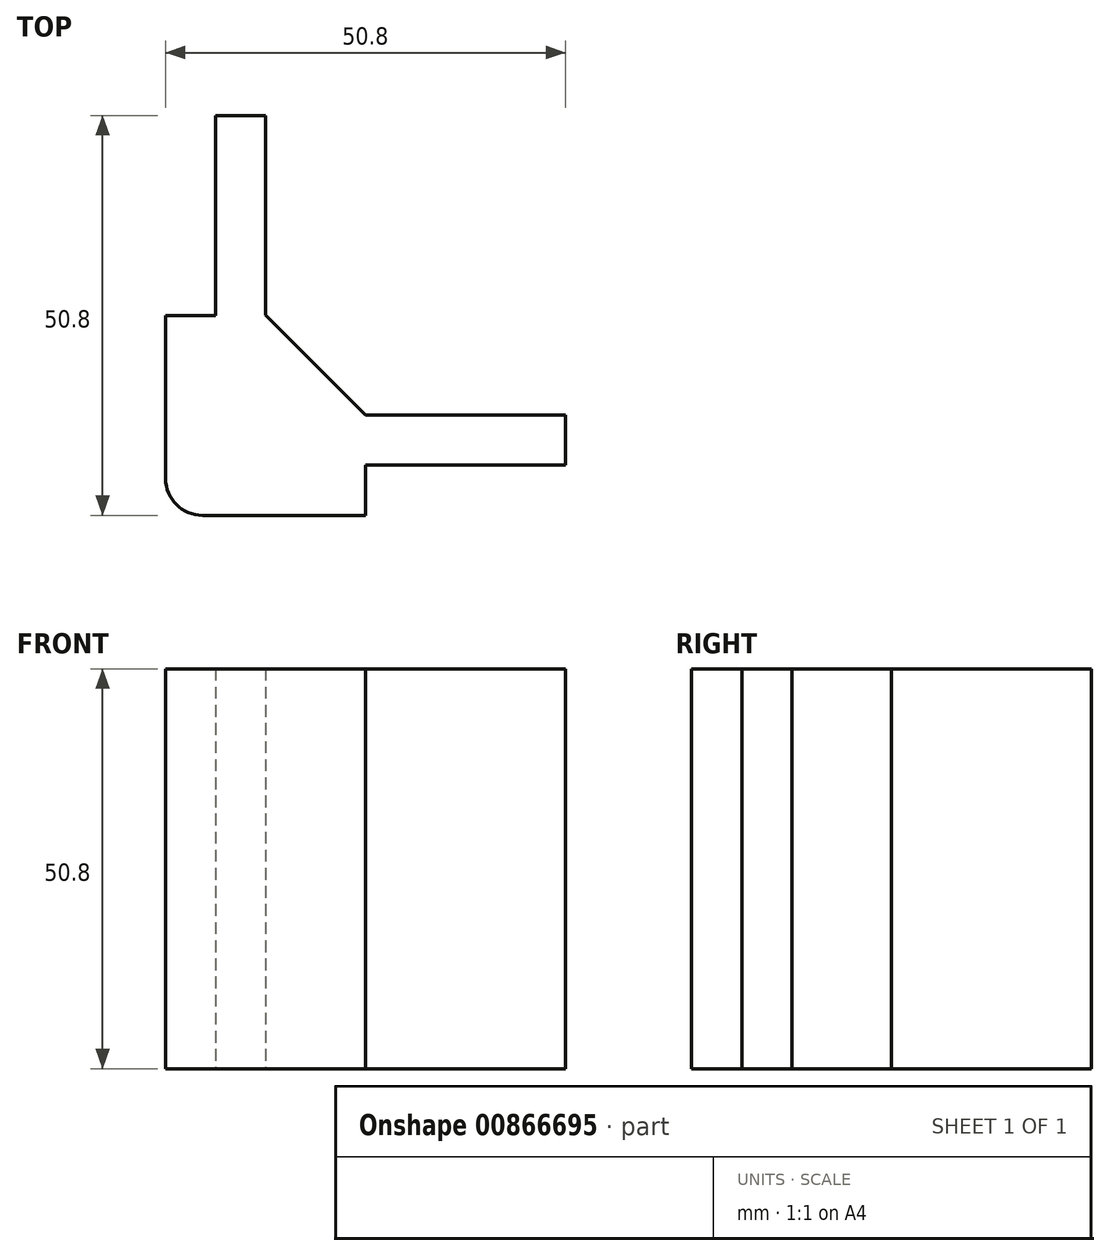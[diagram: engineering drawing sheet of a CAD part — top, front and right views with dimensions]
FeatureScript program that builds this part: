
annotation { "Feature Type Name" : "Feature", "Feature Type Description" : "" }
export const myFeature = defineFeature(function(context is Context, id is Id, definition is map)
    precondition{}
    {
        {
            var Q0;
            Q0=qCreatedBy(makeId("Top.planeOp"),FACE);
            var sketch = newSketch(context, id + "F0", { "sketchPlane" : qUnion([Q0])});
            skLineSegment(sketch, "E0", {"start": v(4.33, 42.13) * mm, "end": v(4.33, 16.73) * mm});
            skLineSegment(sketch, "E1", {"start": v(42.43, 4.08) * mm, "end": v(17.03, 4.08) * mm});
            skLineSegment(sketch, "E2", {"start": v(17.03, 4.08) * mm, "end": v(4.33, 16.73) * mm});
            skLineSegment(sketch, "E3", {"start": v(42.43, -2.27) * mm, "end": v(17.03, -2.27) * mm});
            skLineSegment(sketch, "E4", {"start": v(17.03, -2.27) * mm, "end": v(17.03, -8.67) * mm});
            skLineSegment(sketch, "E5", {"start": v(-2.02, 42.13) * mm, "end": v(-2.02, 16.73) * mm});
            skLineSegment(sketch, "E6", {"start": v(-2.02, 16.73) * mm, "end": v(-8.37, 16.73) * mm});
            skLineSegment(sketch, "E7", {"start": v(-8.37, 16.73) * mm, "end": v(-8.37, -4) * mm});
            skLineSegment(sketch, "E8", {"start": v(17.03, -8.67) * mm, "end": v(-3.7, -8.67) * mm});
            skLineSegment(sketch, "E9", {"start": v(-2.02, 42.13) * mm, "end": v(4.33, 42.13) * mm});
            skLineSegment(sketch, "E10", {"start": v(42.43, -2.27) * mm, "end": v(42.43, 4.08) * mm});
            skPoint(sketch, "E11.visualSharp", {"position": v(-8.37, -8.67) * mm});
            skArc(sketch, "E11.filletArc", {"start": v(-8.37, -4) * mm, "mid": v(-7, -7.3) * mm, "end": v(-3.7, -8.67) * mm});
            skSolve(sketch);
        }
        {
            var Q0;
            Q0 = qSketchRegion(id + "F0", true);
            extrude(context, id + "F1", {"entities" : qUnion([Q0]), "depth" : 50.8 * mm, "offsetDistance" : 25.4 * mm});
        }
        {
            var Q0;
            Q0=makeQuery(id+"F1.opExtrude","CAP_FACE",FACE,{"disambiguationData":[OSD([sQuery(id+"F0.wireOp",EDGE,"E0"),sQuery(id+"F0.wireOp",EDGE,"E1"),sQuery(id+"F0.wireOp",EDGE,"E2"),sQuery(id+"F0.wireOp",EDGE,"E3"),sQuery(id+"F0.wireOp",EDGE,"E4"),sQuery(id+"F0.wireOp",EDGE,"E5"),sQuery(id+"F0.wireOp",EDGE,"E6"),sQuery(id+"F0.wireOp",EDGE,"E7"),sQuery(id+"F0.wireOp",EDGE,"E8"),sQuery(id+"F0.wireOp",EDGE,"E9"),sQuery(id+"F0.wireOp",EDGE,"E10"),sQuery(id+"F0.wireOp",EDGE,"E11.filletArc")])],"isStart":true});
            cPlane(context, id + "F2", {"entities" : qUnion([Q0]), "cplaneType" : CPlaneType.OFFSET, "offset" : 12.7 * mm, "oppositeDirection" : true, "width" : 152.4 * mm, "height" : 152.4 * mm});
        }
    });
